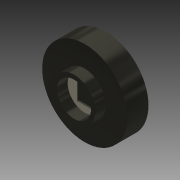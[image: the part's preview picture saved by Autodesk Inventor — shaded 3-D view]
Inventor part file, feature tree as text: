
AUTODESK INVENTOR PART (.ipt)
format: ipt  version: 2015 SP1 (Build 190203100, 203)  size: 125,952 bytes
history: native  units: in
note: dims shown in document units (in); Inventor stores cm internally (conversion verified against a paired STEP export)
features: extrude x5, sketch x5, projected_geometry x3, reference x1
ambient origin geometry x8: Origin, YZ Plane, XZ Plane, XY Plane, X Axis, Y Axis, Z Axis, Center Point
bodies: Solid1 (feature_tree)
feature tree (14):
  extrude  "Lens body"  Depth=0.5in TaperAngle=0.0deg
  extrude  "Ring"  Depth=0.25in TaperAngle=0.0deg
  extrude  "Pit"  Depth=0.25in TaperAngle=0.0deg
  extrude  "Shutters"  Depth=0.35in
  extrude  "Extrusion7"  Depth=0.0197in
  sketch  "Sketch1"  dims[d0=2.0in d1=0.5in d2=0.0in]
  reference  "Reference1"
  sketch  "Sketch2"  dims[d3=1.0in d4=0.25in d5=0.0in]
  projected_geometry  "Projected Loop1"
  sketch  "Sketch5"  dims[d14=0.1in d15=0.25in d16=0.0in]
  projected_geometry  "Projected Loop3"
  sketch  "Sketch6"  dims[d17=0.5in d18=0.35in]
  sketch  "Sketch7"  dims[d19=0.0394in d20=0.0in d21=0.0197in d22=0.0197in d23=0.0in]
  projected_geometry  "Projected Loop4"
